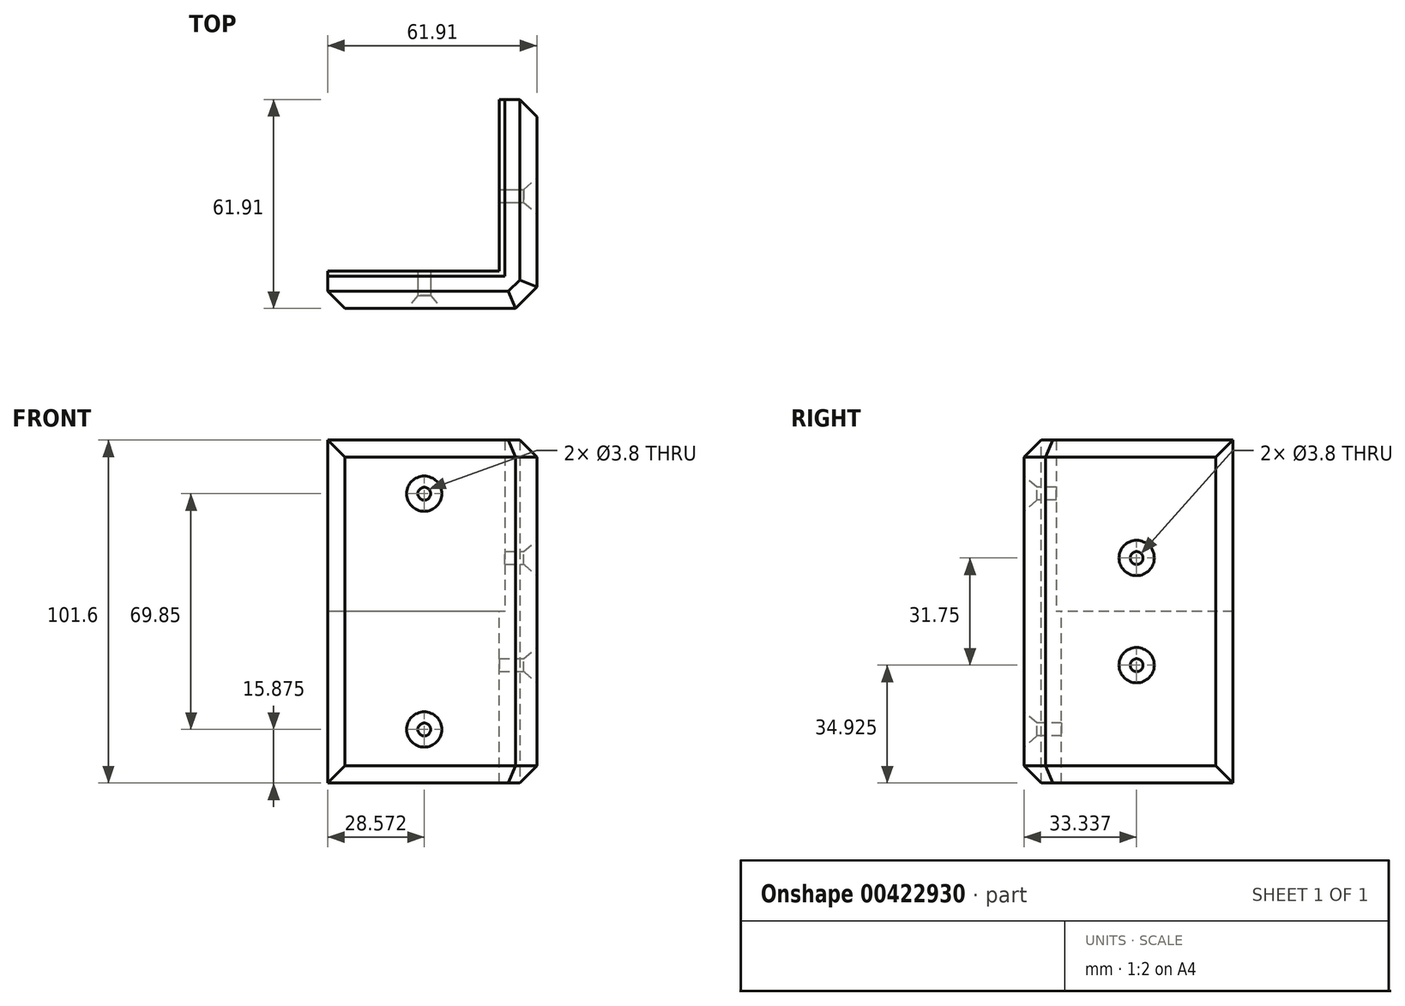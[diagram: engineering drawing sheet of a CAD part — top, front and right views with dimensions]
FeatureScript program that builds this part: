
annotation { "Feature Type Name" : "Feature", "Feature Type Description" : "" }
export const myFeature = defineFeature(function(context is Context, id is Id, definition is map)
    precondition{}
    {
        {
            var Q0;
            Q0=qCreatedBy(makeId("Top.planeOp"),FACE);
            var sketch = newSketch(context, id + "F0", { "sketchPlane" : qUnion([Q0])});
            skLineSegment(sketch, "E0", {"start": v(0, 0) * mm, "end": v(0, 61.91) * mm});
            skLineSegment(sketch, "E1", {"start": v(0, 61.91) * mm, "end": v(-11.11, 61.91) * mm});
            skLineSegment(sketch, "E2", {"start": v(-11.11, 61.91) * mm, "end": v(-11.11, 11.11) * mm});
            skLineSegment(sketch, "E3", {"start": v(-11.11, 11.11) * mm, "end": v(-61.91, 11.11) * mm});
            skLineSegment(sketch, "E4", {"start": v(-61.91, 11.11) * mm, "end": v(-61.91, 0) * mm});
            skLineSegment(sketch, "E5", {"start": v(-61.91, 0) * mm, "end": v(0, 0) * mm});
            skSolve(sketch);
        }
        {
            var Q0;
            Q0=makeQuery(id+"F0.imprint","IMPRINT",FACE,{"disambiguationData":[TD([[makeQuery(id+"F0.imprint","IMPRINT",EDGE,{"derivedFrom":sQuery(id+"F0.wireOp",EDGE,"E0")}),1.0]])]});
            extrude(context, id + "F1", {"entities" : qUnion([Q0]), "oppositeDirection" : true, "depth" : 50.8 * mm});
        }
        {
            var Q0;
            Q0=makeQuery(id+"F1.opExtrude","CAP_FACE",FACE,{"disambiguationData":[OSD([sQuery(id+"F0.wireOp",EDGE,"E0"),sQuery(id+"F0.wireOp",EDGE,"E1"),sQuery(id+"F0.wireOp",EDGE,"E2"),sQuery(id+"F0.wireOp",EDGE,"E3"),sQuery(id+"F0.wireOp",EDGE,"E4"),sQuery(id+"F0.wireOp",EDGE,"E5")])],"isStart":true});
            var sketch = newSketch(context, id + "F2", { "sketchPlane" : qUnion([Q0])});
            skLineSegment(sketch, "E6", {"start": v(0, 61.91) * mm, "end": v(-9.53, 61.91) * mm});
            skLineSegment(sketch, "E7", {"start": v(-9.53, 61.91) * mm, "end": v(-9.53, 9.53) * mm});
            skLineSegment(sketch, "E8", {"start": v(-9.53, 9.53) * mm, "end": v(-61.91, 9.53) * mm});
            skLineSegment(sketch, "E9", {"start": v(-61.91, 9.53) * mm, "end": v(-61.91, 0) * mm});
            skLineSegment(sketch, "E10", {"start": v(-61.91, 0) * mm, "end": v(0, 0) * mm});
            skLineSegment(sketch, "E11", {"start": v(0, 0) * mm, "end": v(0, 61.91) * mm});
            skSolve(sketch);
        }
        {
            var Q0;
            Q0 = qSketchRegion(id + "F2", true);
            extrude(context, id + "F3", {"entities" : qUnion([Q0]), "operationType" : NewBodyOperationType.ADD, "depth" : 50.8 * mm});
        }
        {
            var Q0;
            Q0=makeQuery(id+"F1.opExtrude","SWEPT_FACE",FACE,{"disambiguationData":[OSD([sQuery(id+"F0.wireOp",EDGE,"E0")])]});
            var sketch = newSketch(context, id + "F4", { "sketchPlane" : qUnion([Q0])});
            skCircle(sketch, "E12", {"center": v(33.34, -15.88) * mm, "radius": 3.18 * mm});
            skLineSegment(sketch, "E13", {"start": v(0, 0) * mm, "end": v(61.91, 0) * mm, "construction": true});
            skCircle(sketch, "E14.MirrorC", {"center": v(33.34, 15.87) * mm, "radius": 3.18 * mm});
            skSolve(sketch);
        }
        {
            var Q0;
            Q0=makeQuery(id+"F1.opExtrude","SWEPT_FACE",FACE,{"disambiguationData":[OSD([sQuery(id+"F0.wireOp",EDGE,"E5")])]});
            var sketch = newSketch(context, id + "F5", { "sketchPlane" : qUnion([Q0])});
            skCircle(sketch, "E15", {"center": v(-33.34, -34.93) * mm, "radius": 3.18 * mm});
            skLineSegment(sketch, "E16", {"start": v(0, 0) * mm, "end": v(-61.91, 0) * mm, "construction": true});
            skCircle(sketch, "E17.MirrorC", {"center": v(-33.34, 34.92) * mm, "radius": 3.18 * mm});
            skSolve(sketch);
        }
        {
            var Q0;
            Q0=sQuery(id+"F4.wireOp",VERTEX,"E12.center");
            var Q1;
            Q1=sQuery(id+"F4.wireOp",VERTEX,"gjuDWCIB-VKkJ-KHnt-mKNd-BG35IjNdGhYh.center");
            var Q2;
            Q2=sQuery(id+"F4.wireOp",VERTEX,"a73e6468-ef55-433b-9e5c-053ff8b837081.MirrorC.center");
            var Q3;
            Q3=sQuery(id+"F4.wireOp",VERTEX,"E14.MirrorC.center");
            var Q4;
            Q4=sQuery(id+"F5.wireOp",VERTEX,"E17.MirrorC.center");
            var Q5;
            Q5=sQuery(id+"F5.wireOp",VERTEX,"E15.center");
            var Q6;
            Q6=makeQuery(id+"F1.opExtrude","SWEPT_BODY",BODY,{"disambiguationData":[OSD([sQuery(id+"F0.wireOp",EDGE,"E0"),sQuery(id+"F0.wireOp",EDGE,"E1"),sQuery(id+"F0.wireOp",EDGE,"E2"),sQuery(id+"F0.wireOp",EDGE,"E3"),sQuery(id+"F0.wireOp",EDGE,"E4"),sQuery(id+"F0.wireOp",EDGE,"E5")])]});
            hole(context, id + "F6", {"style" : HoleStyle.C_SINK, "endStyle" : HoleEndStyle.THROUGH, "standardTappedOrClearance" : lookupTablePath({ "standard" : "ANSI", "engagement" : "75%", "pitch" : "24 tpi", "size" : "#10", "type" : "Tapped" }), "standardBlindInLast" : lookupTablePath({ "standard" : "ANSI", "engagement" : "75%", "pitch" : "24 tpi", "size" : "#10", "type" : "Tapped" }), "holeDiameter" : 3.8 * mm, "cSinkDiameter" : 10.44 * mm, "cSinkAngle" : 82 * degree, "showTappedDepth" : true, "isTappedThrough" : true, "tappedDepth" : 12.7 * mm, "tapClearance" : 3, "locations" : qUnion([Q0, Q1, Q2, Q3, Q4, Q5]), "scope" : qUnion([Q6]), "majorDiameter" : 4.83 * mm});
        }
        {
            var Q0;
            Q0=makeQuery(id+"F1.opExtrude","SWEPT_EDGE",EDGE,{"disambiguationData":[OSD([sQuery(id+"F0.wireOp",EDGE,"E0"),sQuery(id+"F0.wireOp",EDGE,"E5")])]});
            chamfer(context, id + "F7", {"entities" : qUnion([Q0]), "width" : 6.35 * mm, "tangentPropagation" : true});
        }
        {
            var Q0;
            Q0=makeQuery(id+"F1.opExtrude","SWEPT_EDGE",EDGE,{"disambiguationData":[OSD([sQuery(id+"F0.wireOp",EDGE,"E4"),sQuery(id+"F0.wireOp",EDGE,"E5")])]});
            var Q1;
            Q1=makeQuery(id+"F1.opExtrude","SWEPT_EDGE",EDGE,{"disambiguationData":[OSD([sQuery(id+"F0.wireOp",EDGE,"E0"),sQuery(id+"F0.wireOp",EDGE,"E1")])]});
            chamfer(context, id + "F8", {"entities" : qUnion([Q0, Q1]), "width" : 5.08 * mm, "tangentPropagation" : true});
        }
        {
            var Q0;
            Q0=makeQuery(id+"F3.opExtrude","CAP_EDGE",EDGE,{"disambiguationData":[OSD([sQuery(id+"F2.wireOp",EDGE,"E10")])],"isStart":false});
            var Q1;
            {var subQ0=sQuery(id+"F2.wireOp",EDGE,"E11");var subQ1=sQuery(id+"F2.wireOp",EDGE,"E10");Q1=makeQuery(id+"F7.opChamfer","BLEND_EDGE",EDGE,{"blendedFrom":[makeQuery(id+"F3.boolean.opBoolean","MERGE",EDGE,{"derivedFrom":[makeQuery(id+"F1.opExtrude","SWEPT_EDGE",EDGE,{"disambiguationData":[OSD([sQuery(id+"F0.wireOp",EDGE,"E0"),sQuery(id+"F0.wireOp",EDGE,"E5")])]}),makeQuery(id+"F3.opExtrude","SWEPT_EDGE",EDGE,{"disambiguationData":[OSD([subQ1,subQ0])]})]}),makeQuery(id+"F3.opExtrude","CAP_FACE",FACE,{"disambiguationData":[OSD([sQuery(id+"F2.wireOp",EDGE,"E6"),sQuery(id+"F2.wireOp",EDGE,"E7"),sQuery(id+"F2.wireOp",EDGE,"E8"),sQuery(id+"F2.wireOp",EDGE,"E9"),subQ1,subQ0])],"isStart":false})],"blendedInto":[makeQuery(id+"F3.opExtrude","CAP_FACE",FACE,{"disambiguationData":[OSD([sQuery(id+"F2.wireOp",EDGE,"E6"),sQuery(id+"F2.wireOp",EDGE,"E7"),sQuery(id+"F2.wireOp",EDGE,"E8"),sQuery(id+"F2.wireOp",EDGE,"E9"),subQ1,subQ0])],"isStart":false})]});}
            var Q2;
            Q2=makeQuery(id+"F3.opExtrude","CAP_EDGE",EDGE,{"disambiguationData":[OSD([sQuery(id+"F2.wireOp",EDGE,"E11")])],"isStart":false});
            var Q3;
            {var subQ0=sQuery(id+"F0.wireOp",EDGE,"E5");var subQ1=sQuery(id+"F0.wireOp",EDGE,"E0");Q3=makeQuery(id+"F7.opChamfer","BLEND_EDGE",EDGE,{"blendedFrom":[makeQuery(id+"F3.boolean.opBoolean","MERGE",EDGE,{"derivedFrom":[makeQuery(id+"F1.opExtrude","SWEPT_EDGE",EDGE,{"disambiguationData":[OSD([subQ1,subQ0])]}),makeQuery(id+"F3.opExtrude","SWEPT_EDGE",EDGE,{"disambiguationData":[OSD([sQuery(id+"F2.wireOp",EDGE,"E10"),sQuery(id+"F2.wireOp",EDGE,"E11")])]})]}),makeQuery(id+"F1.opExtrude","CAP_FACE",FACE,{"disambiguationData":[OSD([subQ1,sQuery(id+"F0.wireOp",EDGE,"E1"),sQuery(id+"F0.wireOp",EDGE,"E2"),sQuery(id+"F0.wireOp",EDGE,"E3"),sQuery(id+"F0.wireOp",EDGE,"E4"),subQ0])],"isStart":false})],"blendedInto":[makeQuery(id+"F1.opExtrude","CAP_FACE",FACE,{"disambiguationData":[OSD([subQ1,sQuery(id+"F0.wireOp",EDGE,"E1"),sQuery(id+"F0.wireOp",EDGE,"E2"),sQuery(id+"F0.wireOp",EDGE,"E3"),sQuery(id+"F0.wireOp",EDGE,"E4"),subQ0])],"isStart":false})]});}
            var Q4;
            Q4=makeQuery(id+"F1.opExtrude","CAP_EDGE",EDGE,{"disambiguationData":[OSD([sQuery(id+"F0.wireOp",EDGE,"E5")])],"isStart":false});
            var Q5;
            Q5=makeQuery(id+"F1.opExtrude","CAP_EDGE",EDGE,{"disambiguationData":[OSD([sQuery(id+"F0.wireOp",EDGE,"E0")])],"isStart":false});
            chamfer(context, id + "F9", {"entities" : qUnion([Q0, Q1, Q2, Q3, Q4, Q5]), "width" : 5.08 * mm, "tangentPropagation" : true});
        }
    });
